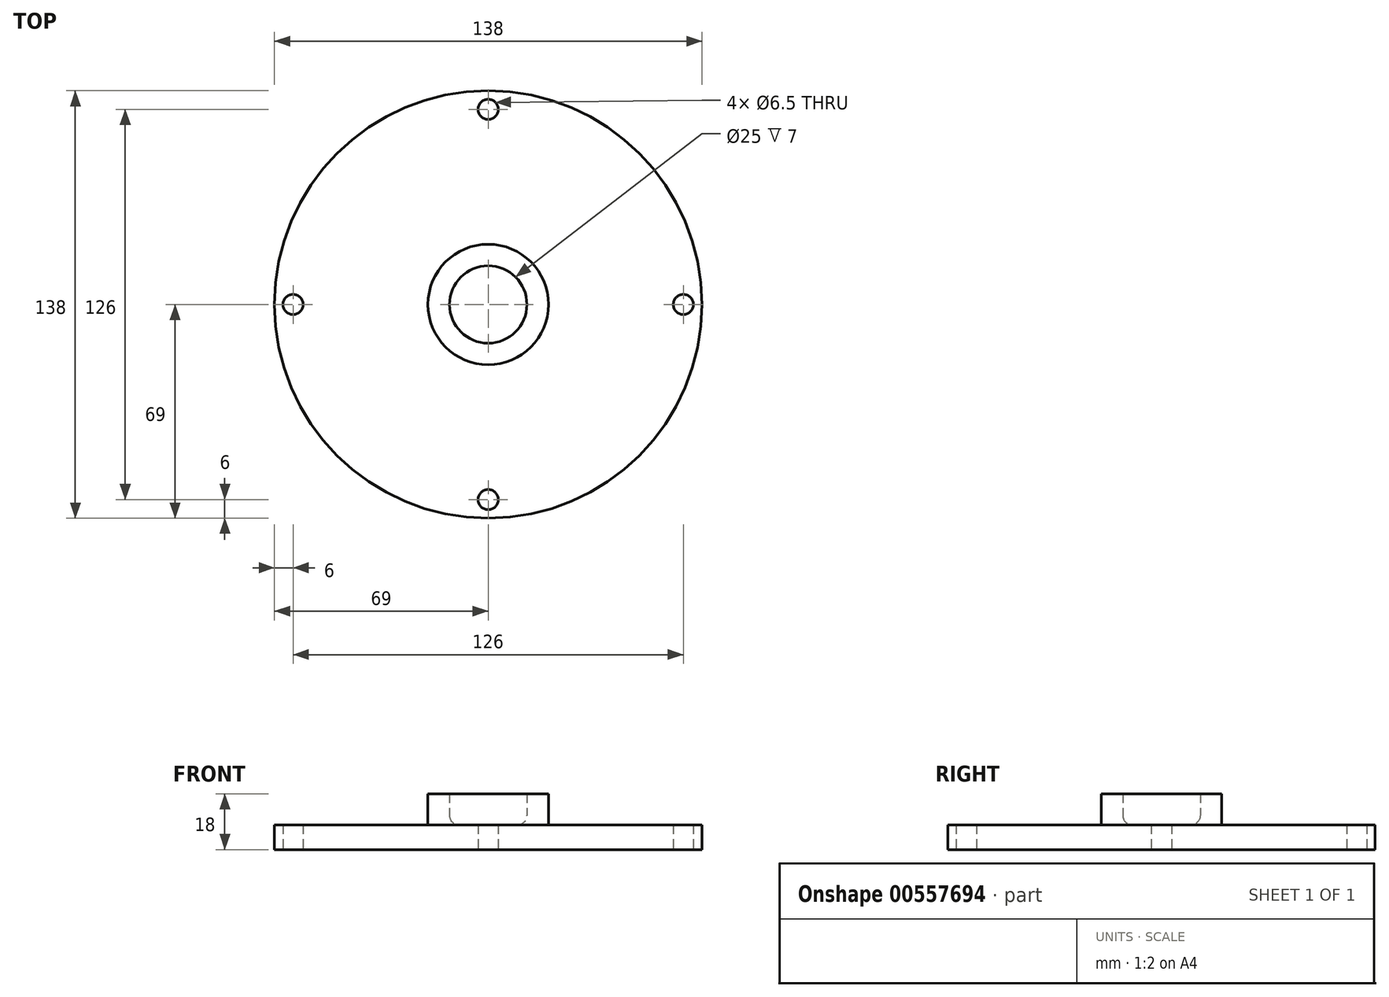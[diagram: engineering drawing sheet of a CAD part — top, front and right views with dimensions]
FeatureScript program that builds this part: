
annotation { "Feature Type Name" : "Feature", "Feature Type Description" : "" }
export const myFeature = defineFeature(function(context is Context, id is Id, definition is map)
    precondition{}
    {
        {
            var Q0;
            Q0=qCreatedBy(makeId("Top.planeOp"),FACE);
            var sketch = newSketch(context, id + "F0", { "sketchPlane" : qUnion([Q0])});
            skCircle(sketch, "E0", {"center": v(0, 0) * mm, "radius": 69 * mm});
            skCircle(sketch, "E1", {"center": v(0, 63) * mm, "radius": 3.25 * mm});
            skCircle(sketch, "E2.1.0", {"center": v(-63, 0) * mm, "radius": 3.25 * mm});
            skCircle(sketch, "E2.2.0", {"center": v(0, -63) * mm, "radius": 3.25 * mm});
            skCircle(sketch, "E2.3.0", {"center": v(63, 0) * mm, "radius": 3.25 * mm});
            skSolve(sketch);
        }
        {
            var Q0;
            Q0=makeQuery(id+"F0.imprint","IMPRINT",FACE,{"disambiguationData":[TD([[makeQuery(id+"F0.imprint","IMPRINT",EDGE,{"derivedFrom":sQuery(id+"F0.wireOp",EDGE,"E0")}),1.0]])]});
            extrude(context, id + "F1", {"entities" : qUnion([Q0]), "depth" : 8 * mm, "offsetDistance" : 25 * mm});
        }
        {
            var Q0;
            Q0=makeQuery(id+"F1.opExtrude","CAP_FACE",FACE,{"disambiguationData":[OSD([sQuery(id+"F0.wireOp",EDGE,"E0"),sQuery(id+"F0.wireOp",EDGE,"E1"),sQuery(id+"F0.wireOp",EDGE,"E2.1.0"),sQuery(id+"F0.wireOp",EDGE,"E2.2.0"),sQuery(id+"F0.wireOp",EDGE,"E2.3.0")])],"isStart":false});
            var sketch = newSketch(context, id + "F2", { "sketchPlane" : qUnion([Q0])});
            skCircle(sketch, "E3", {"center": v(0, 0) * mm, "radius": 19.45 * mm});
            skCircle(sketch, "E4", {"center": v(0, 0) * mm, "radius": 12.5 * mm});
            skSolve(sketch);
        }
        {
            var Q0;
            Q0=makeQuery(id+"F2.imprint","IMPRINT",FACE,{"disambiguationData":[TD([[makeQuery(id+"F2.imprint","IMPRINT",EDGE,{"derivedFrom":sQuery(id+"F2.wireOp",EDGE,"E3")}),1.0]])]});
            extrude(context, id + "F3", {"entities" : qUnion([Q0]), "operationType" : NewBodyOperationType.ADD, "depth" : 10 * mm, "offsetDistance" : 25 * mm});
        }
        {
            var Q0;
            Q0=makeQuery(id+"F3.opExtrude","CAP_EDGE",EDGE,{"disambiguationData":[OSD([sQuery(id+"F2.wireOp",EDGE,"E4")])],"isStart":true});
            fillet(context, id + "F4", {"entities" : qUnion([Q0]), "radius" : 3 * mm, "tangentPropagation" : true, "allowEdgeOverflow" : false});
        }
    });
